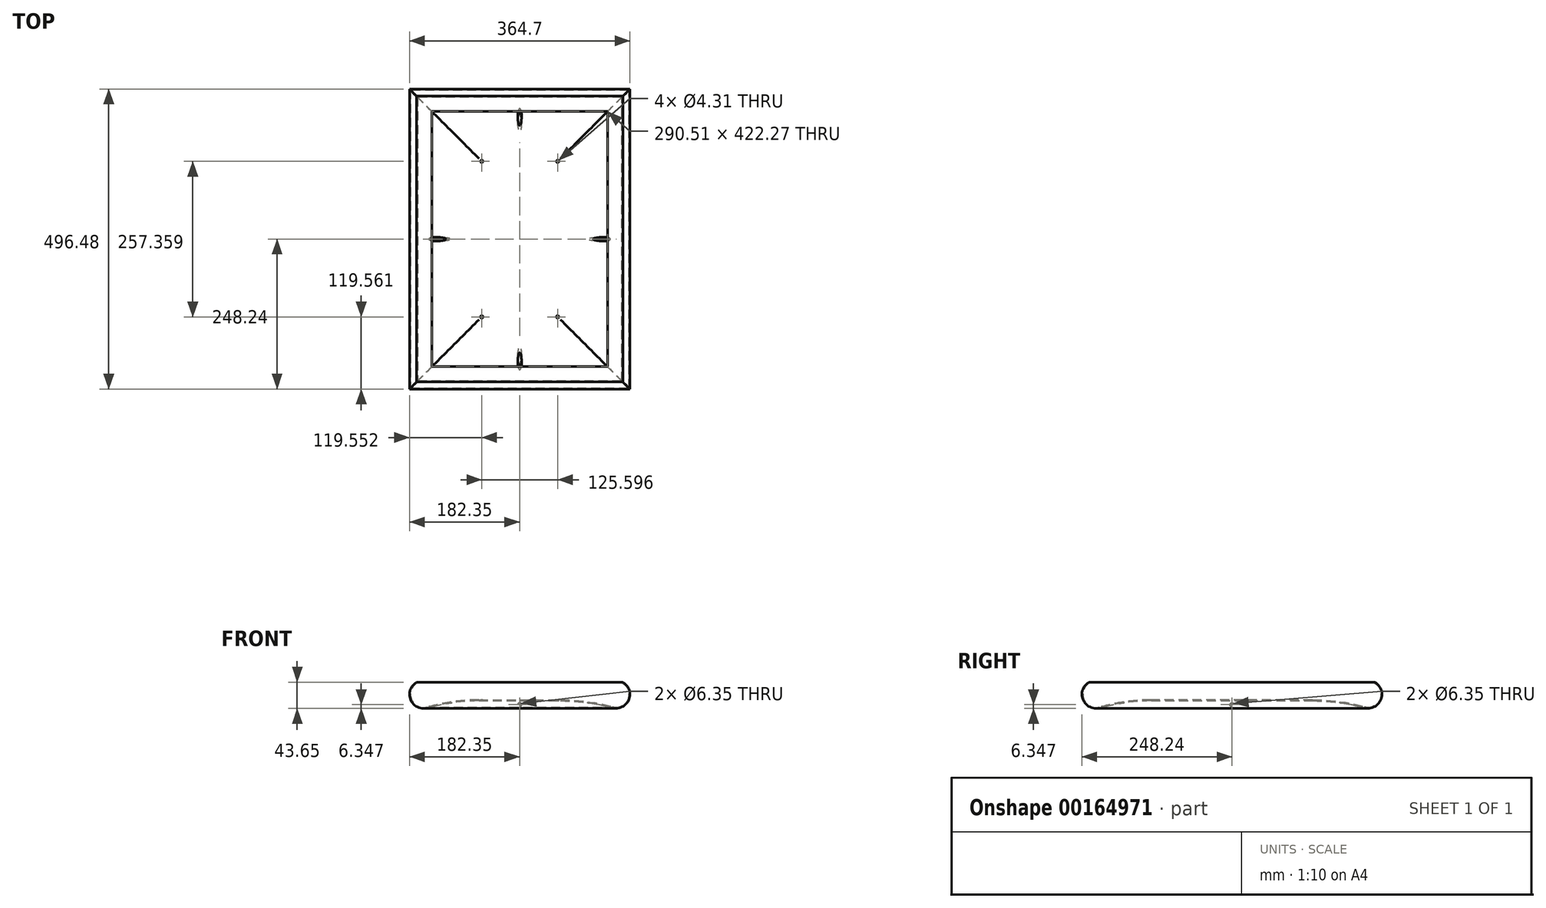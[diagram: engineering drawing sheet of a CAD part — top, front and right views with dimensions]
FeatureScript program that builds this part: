
annotation { "Feature Type Name" : "Feature", "Feature Type Description" : "" }
export const myFeature = defineFeature(function(context is Context, id is Id, definition is map)
    precondition{}
    {
        {
            var Q0;
            Q0=qCreatedBy(makeId("Top.planeOp"),FACE);
            var sketch = newSketch(context, id + "F0", { "sketchPlane" : qUnion([Q0])});
            skLineSegment(sketch, "E0.bottom", {"start": v(170.66, 236.54) * mm, "end": v(-170.66, 236.54) * mm});
            skLineSegment(sketch, "E0.top", {"start": v(170.66, -236.54) * mm, "end": v(-170.66, -236.54) * mm});
            skLineSegment(sketch, "E0.left", {"start": v(170.66, 236.54) * mm, "end": v(170.66, -236.54) * mm});
            skLineSegment(sketch, "E0.right", {"start": v(-170.66, 236.54) * mm, "end": v(-170.66, -236.54) * mm});
            skPoint(sketch, "E0.middle", {"position": v(0, 0) * mm});
            skSolve(sketch);
        }
        {
            var Q0;
            Q0=qSketchRegion(id+"F0",true);
            extrude(context, id + "F1", {"entities" : qUnion([Q0]), "depth" : 0.8 * mm});
        }
        {
            var Q0;
            Q0=makeQuery(id+"F1.opExtrude","SWEPT_FACE",FACE,{"disambiguationData":[OSD([sQuery(id+"F0.wireOp",EDGE,"E0.top")])]});
            var sketch = newSketch(context, id + "F2", { "sketchPlane" : qUnion([Q0])});
            skArc(sketch, "E1", {"start": v(152.58, -41.98) * mm, "mid": v(180.5, -28.57) * mm, "end": v(170.66, 0.8) * mm});
            skArc(sketch, "E2", {"start": v(153.01, -40.45) * mm, "mid": v(179.28, -27.4) * mm, "end": v(168.79, 0) * mm});
            skLineSegment(sketch, "E3", {"start": v(0, 0) * mm, "end": v(0, -28.57) * mm, "construction": true});
            skLineSegment(sketch, "E4.bottom", {"start": v(0, -28.57) * mm, "end": v(67.56, -28.57) * mm});
            skLineSegment(sketch, "E4.top", {"start": v(0, -30.16) * mm, "end": v(67.56, -30.16) * mm});
            skLineSegment(sketch, "E4.left", {"start": v(0, -28.57) * mm, "end": v(0, -30.16) * mm});
            skLineSegment(sketch, "E4.right", {"start": v(67.56, -28.58) * mm, "end": v(67.56, -30.16) * mm, "construction": true});
            skLineSegment(sketch, "E5", {"start": v(0, -30.16) * mm, "end": v(0, -42.86) * mm, "construction": true});
            skLineSegment(sketch, "E6", {"start": v(0, -42.86) * mm, "end": v(158.96, -42.86) * mm, "construction": true});
            skArc(sketch, "E7", {"start": v(153.01, -40.45) * mm, "mid": v(110.7, -31.56) * mm, "end": v(67.56, -28.58) * mm});
            skArc(sketch, "E8", {"start": v(152.58, -41.98) * mm, "mid": v(110.48, -33.13) * mm, "end": v(67.56, -30.16) * mm});
            skLineSegment(sketch, "E9", {"start": v(170.66, 0.8) * mm, "end": v(145.26, 15.46) * mm, "construction": true});
            skLineSegment(sketch, "E10", {"start": v(145.26, 15.46) * mm, "end": v(145.26, 0.8) * mm, "construction": true});
            skLineSegment(sketch, "E11", {"start": v(145.26, 0.8) * mm, "end": v(170.66, 0.8) * mm, "construction": true});
            skLineSegment(sketch, "E12", {"start": v(170.66, 0.8) * mm, "end": v(170.66, 0) * mm});
            skLineSegment(sketch, "E13", {"start": v(170.66, 0) * mm, "end": v(168.79, 0) * mm});
            skSolve(sketch);
        }
        {
            var Q0;
            Q0=makeQuery(id+"F2.imprint","IMPRINT",FACE,{"disambiguationData":[TD([[makeQuery(id+"F2.imprint","IMPRINT",EDGE,{"derivedFrom":sQuery(id+"F2.wireOp",EDGE,"E1")}),1.0]])]});
            var Q1;
            Q1=makeQuery(id+"F1.opExtrude","CAP_EDGE",EDGE,{"disambiguationData":[OSD([sQuery(id+"F0.wireOp",EDGE,"E0.left")])],"isStart":false});
            var Q2;
            Q2=makeQuery(id+"F1.opExtrude","CAP_EDGE",EDGE,{"disambiguationData":[OSD([sQuery(id+"F0.wireOp",EDGE,"E0.bottom")])],"isStart":false});
            var Q3;
            Q3=makeQuery(id+"F1.opExtrude","CAP_EDGE",EDGE,{"disambiguationData":[OSD([sQuery(id+"F0.wireOp",EDGE,"E0.right")])],"isStart":false});
            var Q4;
            Q4=makeQuery(id+"F1.opExtrude","CAP_EDGE",EDGE,{"disambiguationData":[OSD([sQuery(id+"F0.wireOp",EDGE,"E0.top")])],"isStart":false});
            sweep(context, id + "F3", {"operationType" : NewBodyOperationType.ADD, "profiles" : qUnion([Q0]), "path" : qUnion([Q1, Q2, Q3, Q4])});
        }
        {
            var Q0;
            Q0=makeQuery(id+"F1.opExtrude","CAP_FACE",FACE,{"disambiguationData":[OSD([sQuery(id+"F0.wireOp",EDGE,"E0.bottom"),sQuery(id+"F0.wireOp",EDGE,"E0.top"),sQuery(id+"F0.wireOp",EDGE,"E0.left"),sQuery(id+"F0.wireOp",EDGE,"E0.right")])],"isStart":false});
            var sketch = newSketch(context, id + "F4", { "sketchPlane" : qUnion([Q0])});
            skLineSegment(sketch, "E14.bottom", {"start": v(145.26, 211.14) * mm, "end": v(-145.26, 211.14) * mm});
            skLineSegment(sketch, "E14.top", {"start": v(145.26, -211.14) * mm, "end": v(-145.26, -211.14) * mm});
            skLineSegment(sketch, "E14.left", {"start": v(145.26, 211.14) * mm, "end": v(145.26, -211.14) * mm});
            skLineSegment(sketch, "E14.right", {"start": v(-145.26, 211.14) * mm, "end": v(-145.26, -211.14) * mm});
            skPoint(sketch, "E14.middle", {"position": v(0, 0) * mm});
            skLineSegment(sketch, "E15.bottom", {"start": v(145.26, 211.14) * mm, "end": v(170.66, 211.14) * mm, "construction": true});
            skLineSegment(sketch, "E15.top", {"start": v(145.26, 236.54) * mm, "end": v(170.66, 236.54) * mm, "construction": true});
            skLineSegment(sketch, "E15.left", {"start": v(145.26, 211.14) * mm, "end": v(145.26, 236.54) * mm, "construction": true});
            skLineSegment(sketch, "E15.right", {"start": v(170.66, 211.14) * mm, "end": v(170.66, 236.54) * mm, "construction": true});
            skSolve(sketch);
        }
        {
            var Q0;
            Q0 = qSketchRegion(id + "F4", true);
            var Q1;
            Q1=makeQuery(id+"F1.opExtrude","CAP_FACE",FACE,{"disambiguationData":[OSD([sQuery(id+"F0.wireOp",EDGE,"E0.bottom"),sQuery(id+"F0.wireOp",EDGE,"E0.top"),sQuery(id+"F0.wireOp",EDGE,"E0.left"),sQuery(id+"F0.wireOp",EDGE,"E0.right")])],"isStart":true});
            extrude(context, id + "F5", {"entities" : qUnion([Q0]), "operationType" : NewBodyOperationType.REMOVE, "endBound" : BoundingType.UP_TO_SURFACE, "oppositeDirection" : true, "endBoundEntityFace" : qUnion([Q1]), "depth" : 25.4 * mm});
        }
        {
            var Q0;
            Q0=qCreatedBy(makeId("Front.planeOp"),FACE);
            var sketch = newSketch(context, id + "F6", { "sketchPlane" : qUnion([Q0])});
            skLineSegment(sketch, "E16", {"start": v(0, -30.16) * mm, "end": v(0, -36.51) * mm, "construction": true});
            skCircle(sketch, "E17", {"center": v(0, -36.51) * mm, "radius": 3.18 * mm});
            skSolve(sketch);
        }
        {
            var Q0;
            Q0 = qSketchRegion(id + "F6", true);
            var Q1;
            Q1=makeQuery(id+"F3.opSweep","SWEPT_FACE",FACE,{"disambiguationData":[OSD([sQuery(id+"F0.wireOp",EDGE,"E0.bottom"),sQuery(id+"F2.wireOp",EDGE,"E2")])]});
            var Q2;
            Q2=makeQuery(id+"F3.opSweep","SWEPT_FACE",FACE,{"disambiguationData":[OSD([sQuery(id+"F0.wireOp",EDGE,"E0.top"),sQuery(id+"F2.wireOp",EDGE,"E2")])]});
            extrude(context, id + "F7", {"entities" : qUnion([Q0]), "operationType" : NewBodyOperationType.REMOVE, "endBound" : BoundingType.UP_TO_SURFACE, "oppositeDirection" : true, "endBoundEntityFace" : qUnion([Q1]), "depth" : 25.4 * mm, "hasSecondDirection" : true, "secondDirectionBound" : SecondDirectionBoundingType.UP_TO_SURFACE, "secondDirectionOppositeDirection" : false, "secondDirectionBoundEntityFace" : qUnion([Q2]), "secondDirectionDepth" : 25.4 * mm});
        }
        {
            var Q0;
            Q0=qCreatedBy(makeId("Right.planeOp"),FACE);
            var sketch = newSketch(context, id + "F8", { "sketchPlane" : qUnion([Q0])});
            skLineSegment(sketch, "E18", {"start": v(0, -30.16) * mm, "end": v(0, -36.51) * mm, "construction": true});
            skCircle(sketch, "E19", {"center": v(0, -36.51) * mm, "radius": 3.18 * mm});
            skSolve(sketch);
        }
        {
            var Q0;
            Q0 = qSketchRegion(id + "F8", true);
            var Q1;
            Q1=makeQuery(id+"F3.opSweep","SWEPT_FACE",FACE,{"disambiguationData":[OSD([sQuery(id+"F0.wireOp",EDGE,"E0.right"),sQuery(id+"F2.wireOp",EDGE,"E2")])]});
            var Q2;
            Q2=makeQuery(id+"F3.opSweep","SWEPT_FACE",FACE,{"disambiguationData":[OSD([sQuery(id+"F0.wireOp",EDGE,"E0.left"),sQuery(id+"F2.wireOp",EDGE,"E2")])]});
            extrude(context, id + "F9", {"entities" : qUnion([Q0]), "operationType" : NewBodyOperationType.REMOVE, "endBound" : BoundingType.UP_TO_SURFACE, "oppositeDirection" : true, "endBoundEntityFace" : qUnion([Q1]), "depth" : 25.4 * mm, "hasSecondDirection" : true, "secondDirectionBound" : SecondDirectionBoundingType.UP_TO_SURFACE, "secondDirectionOppositeDirection" : false, "secondDirectionBoundEntityFace" : qUnion([Q2]), "secondDirectionDepth" : 25.4 * mm});
        }
        {
            var Q0;
            Q0=makeQuery(id+"F3.opSweep","SWEPT_FACE",FACE,{"disambiguationData":[OSD([sQuery(id+"F0.wireOp",EDGE,"E0.left"),sQuery(id+"F2.wireOp",EDGE,"E4.top")])]});
            var sketch = newSketch(context, id + "F10", { "sketchPlane" : qUnion([Q0])});
            skLineSegment(sketch, "E20", {"start": v(0, 133.44) * mm, "end": v(0, -133.44) * mm, "construction": true});
            skLineSegment(sketch, "E21.bottom", {"start": v(67.56, 133.44) * mm, "end": v(62.8, 133.44) * mm, "construction": true});
            skLineSegment(sketch, "E21.top", {"start": v(67.56, 128.68) * mm, "end": v(62.8, 128.68) * mm, "construction": true});
            skLineSegment(sketch, "E21.left", {"start": v(67.56, 133.44) * mm, "end": v(67.56, 128.68) * mm, "construction": true});
            skLineSegment(sketch, "E21.right", {"start": v(62.8, 133.44) * mm, "end": v(62.8, 128.68) * mm, "construction": true});
            skLineSegment(sketch, "E22.bottom", {"start": v(62.8, 128.68) * mm, "end": v(-62.8, 128.68) * mm, "construction": true});
            skLineSegment(sketch, "E22.top", {"start": v(62.8, -128.68) * mm, "end": v(-62.8, -128.68) * mm, "construction": true});
            skLineSegment(sketch, "E22.left", {"start": v(62.8, 128.68) * mm, "end": v(62.8, -128.68) * mm, "construction": true});
            skLineSegment(sketch, "E22.right", {"start": v(-62.8, 128.68) * mm, "end": v(-62.8, -128.68) * mm, "construction": true});
            skPoint(sketch, "E22.middle", {"position": v(0, 0) * mm});
            skCircle(sketch, "E23", {"center": v(-62.8, 128.68) * mm, "radius": 2.15 * mm});
            skCircle(sketch, "E24", {"center": v(62.8, 128.68) * mm, "radius": 2.15 * mm});
            skCircle(sketch, "E25", {"center": v(62.8, -128.68) * mm, "radius": 2.15 * mm});
            skCircle(sketch, "E26", {"center": v(-62.8, -128.68) * mm, "radius": 2.15 * mm});
            skSolve(sketch);
        }
        {
            var Q0;
            Q0 = qSketchRegion(id + "F10", true);
            var Q1;
            Q1=makeQuery(id+"F3.opSweep","SWEPT_FACE",FACE,{"disambiguationData":[OSD([sQuery(id+"F0.wireOp",EDGE,"E0.left"),sQuery(id+"F2.wireOp",EDGE,"E4.bottom")])]});
            extrude(context, id + "F11", {"entities" : qUnion([Q0]), "operationType" : NewBodyOperationType.REMOVE, "endBound" : BoundingType.UP_TO_SURFACE, "oppositeDirection" : true, "endBoundEntityFace" : qUnion([Q1]), "depth" : 25.4 * mm});
        }
    });
